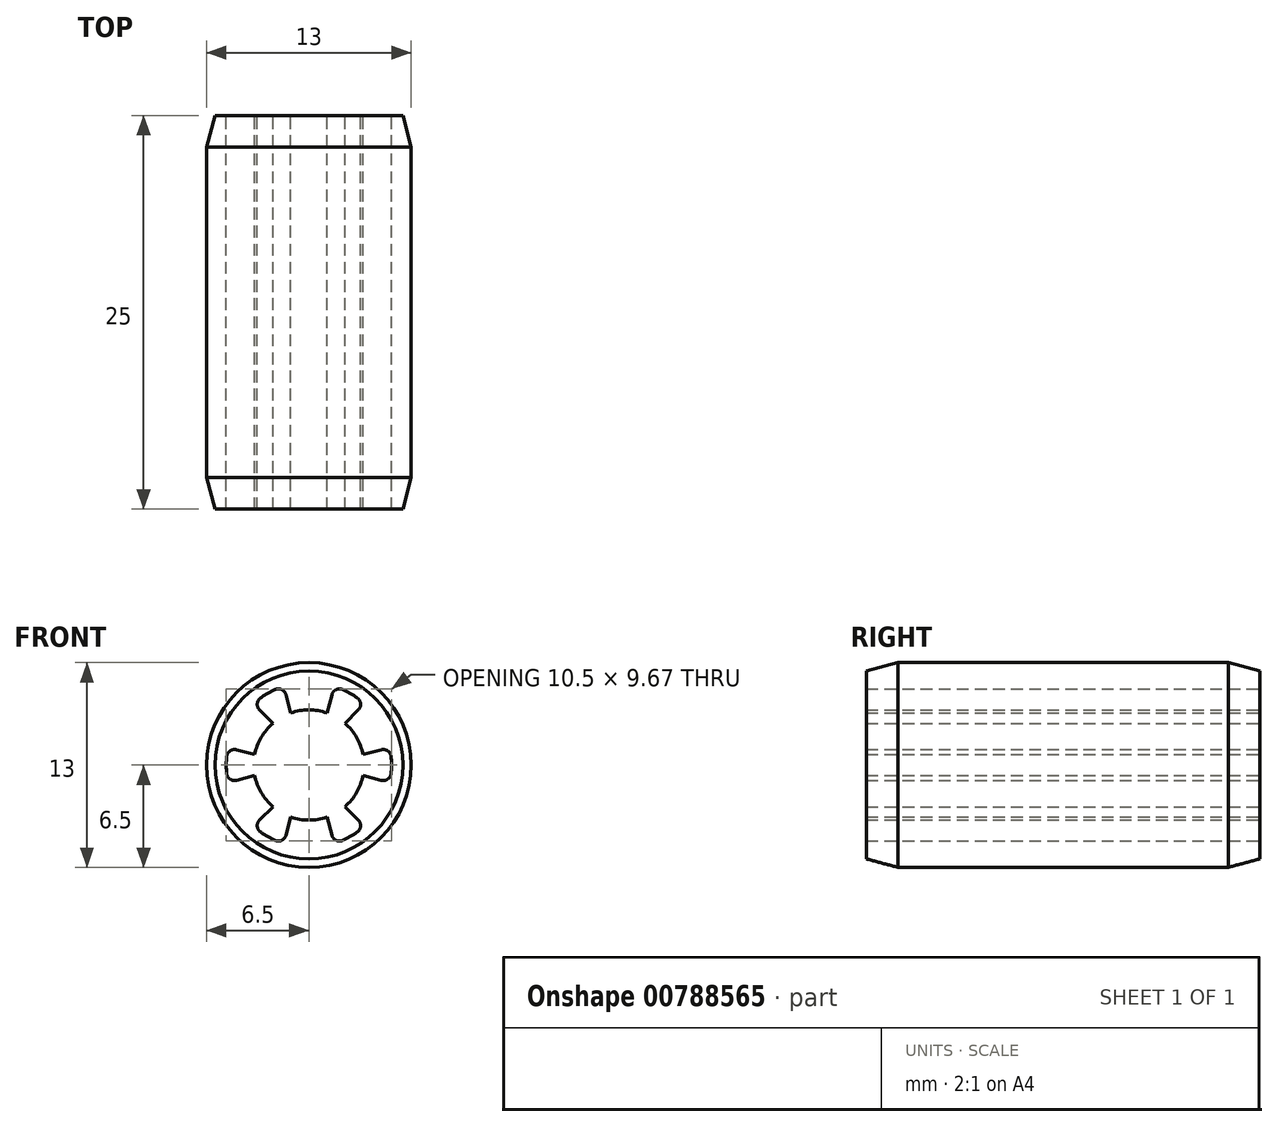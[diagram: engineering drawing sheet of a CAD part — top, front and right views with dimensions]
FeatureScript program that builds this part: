
annotation { "Feature Type Name" : "Feature", "Feature Type Description" : "" }
export const myFeature = defineFeature(function(context is Context, id is Id, definition is map)
    precondition{}
    {
        {
            var Q0;
            Q0=qCreatedBy(makeId("Front.planeOp"),FACE);
            var sketch = newSketch(context, id + "F0", { "sketchPlane" : qUnion([Q0])});
            skCircle(sketch, "E0", {"center": v(0, 0) * mm, "radius": 6.5 * mm});
            skCircle(sketch, "E1", {"center": v(0, 0) * mm, "radius": 5.25 * mm});
            skArc(sketch, "E2", {"start": v(-2.29, 2.65) * mm, "mid": v(-3.03, 1.75) * mm, "end": v(-3.44, 0.66) * mm});
            skLineSegment(sketch, "E3", {"start": v(1.6, 5) * mm, "end": v(1.15, 3.3) * mm});
            skLineSegment(sketch, "E4", {"start": v(-1.6, 5) * mm, "end": v(-1.15, 3.3) * mm});
            skLineSegment(sketch, "E5.1.0", {"start": v(-5.13, 1.11) * mm, "end": v(-3.44, 0.66) * mm});
            skLineSegment(sketch, "E5.1.1", {"start": v(-3.53, 3.89) * mm, "end": v(-2.29, 2.65) * mm});
            skLineSegment(sketch, "E5.2.0", {"start": v(-3.53, -3.89) * mm, "end": v(-2.29, -2.65) * mm});
            skLineSegment(sketch, "E5.2.1", {"start": v(-5.13, -1.11) * mm, "end": v(-3.44, -0.66) * mm});
            skLineSegment(sketch, "E5.3.0", {"start": v(1.6, -5) * mm, "end": v(1.15, -3.3) * mm});
            skLineSegment(sketch, "E5.3.1", {"start": v(-1.6, -5) * mm, "end": v(-1.15, -3.3) * mm});
            skLineSegment(sketch, "E5.4.0", {"start": v(5.13, -1.11) * mm, "end": v(3.44, -0.66) * mm});
            skLineSegment(sketch, "E5.4.1", {"start": v(3.53, -3.89) * mm, "end": v(2.29, -2.65) * mm});
            skLineSegment(sketch, "E5.5.0", {"start": v(3.53, 3.89) * mm, "end": v(2.29, 2.65) * mm});
            skLineSegment(sketch, "E5.5.1", {"start": v(5.13, 1.11) * mm, "end": v(3.44, 0.66) * mm});
            skArc(sketch, "E6.trimOffspring", {"start": v(1.15, 3.3) * mm, "mid": v(0, 3.5) * mm, "end": v(-1.15, 3.3) * mm});
            skArc(sketch, "E7.trimOffspring", {"start": v(3.44, 0.66) * mm, "mid": v(3.03, 1.75) * mm, "end": v(2.29, 2.65) * mm});
            skArc(sketch, "E8.trimOffspring", {"start": v(2.29, -2.65) * mm, "mid": v(3.03, -1.75) * mm, "end": v(3.44, -0.66) * mm});
            skArc(sketch, "E9.trimOffspring", {"start": v(-1.15, -3.3) * mm, "mid": v(0, -3.5) * mm, "end": v(1.15, -3.3) * mm});
            skArc(sketch, "E10.trimOffspring", {"start": v(-3.44, -0.66) * mm, "mid": v(-3.03, -1.75) * mm, "end": v(-2.29, -2.65) * mm});
            skSolve(sketch);
        }
        {
            var Q0;
            Q0=makeQuery(id+"F0.imprint","IMPRINT",FACE,{"disambiguationData":[TD([[makeQuery(id+"F0.imprint","IMPRINT",EDGE,{"derivedFrom":sQuery(id+"F0.wireOp",EDGE,"E0")}),1.0]])]});
            var Q1;
            {var subQ0=sQuery(id+"F0.wireOp",EDGE,"E3");Q1=makeQuery(id+"F0.imprint","IMPRINT",FACE,{"disambiguationData":[TD([[makeQuery(id+"F0.imprint","IMPRINT",EDGE,{"derivedFrom":subQ0}),-1.0]])]});}
            var Q2;
            {var subQ0=sQuery(id+"F0.wireOp",EDGE,"E5.5.0");Q2=makeQuery(id+"F0.imprint","IMPRINT",FACE,{"disambiguationData":[TD([[makeQuery(id+"F0.imprint","IMPRINT",EDGE,{"derivedFrom":subQ0}),1.0]])]});}
            var Q3;
            {var subQ0=sQuery(id+"F0.wireOp",EDGE,"E5.4.0");Q3=makeQuery(id+"F0.imprint","IMPRINT",FACE,{"disambiguationData":[TD([[makeQuery(id+"F0.imprint","IMPRINT",EDGE,{"derivedFrom":subQ0}),1.0]])]});}
            var Q4;
            {var subQ0=sQuery(id+"F0.wireOp",EDGE,"E5.3.0");Q4=makeQuery(id+"F0.imprint","IMPRINT",FACE,{"disambiguationData":[TD([[makeQuery(id+"F0.imprint","IMPRINT",EDGE,{"derivedFrom":subQ0}),1.0]])]});}
            var Q5;
            {var subQ0=sQuery(id+"F0.wireOp",EDGE,"E5.2.0");Q5=makeQuery(id+"F0.imprint","IMPRINT",FACE,{"disambiguationData":[TD([[makeQuery(id+"F0.imprint","IMPRINT",EDGE,{"derivedFrom":subQ0}),1.0]])]});}
            var Q6;
            Q6=makeQuery(id+"F0.imprint","IMPRINT",FACE,{"disambiguationData":[TD([[makeQuery(id+"F0.imprint","IMPRINT",EDGE,{"derivedFrom":sQuery(id+"F0.wireOp",EDGE,"E2")}),-1.0]])]});
            extrude(context, id + "F1", {"entities" : qUnion([Q0, Q1, Q2, Q3, Q4, Q5, Q6]), "depth" : 25 * mm, "offsetDistance" : 25 * mm});
        }
        {
            var Q0;
            Q0=makeQuery(id+"F1.opExtrude","SWEPT_EDGE",EDGE,{"disambiguationData":[OSD([sQuery(id+"F0.wireOp",EDGE,"E1"),sQuery(id+"F0.wireOp",EDGE,"E5.1.1")])]});
            var Q1;
            Q1=makeQuery(id+"F1.opExtrude","SWEPT_EDGE",EDGE,{"disambiguationData":[OSD([sQuery(id+"F0.wireOp",EDGE,"E1"),sQuery(id+"F0.wireOp",EDGE,"E4")])]});
            var Q2;
            Q2=makeQuery(id+"F1.opExtrude","SWEPT_EDGE",EDGE,{"disambiguationData":[OSD([sQuery(id+"F0.wireOp",EDGE,"E1"),sQuery(id+"F0.wireOp",EDGE,"E3")])]});
            var Q3;
            Q3=makeQuery(id+"F1.opExtrude","SWEPT_EDGE",EDGE,{"disambiguationData":[OSD([sQuery(id+"F0.wireOp",EDGE,"E1"),sQuery(id+"F0.wireOp",EDGE,"E5.5.0")])]});
            var Q4;
            Q4=makeQuery(id+"F1.opExtrude","SWEPT_EDGE",EDGE,{"disambiguationData":[OSD([sQuery(id+"F0.wireOp",EDGE,"E1"),sQuery(id+"F0.wireOp",EDGE,"E5.5.1")])]});
            var Q5;
            Q5=makeQuery(id+"F1.opExtrude","SWEPT_EDGE",EDGE,{"disambiguationData":[OSD([sQuery(id+"F0.wireOp",EDGE,"E1"),sQuery(id+"F0.wireOp",EDGE,"E5.4.0")])]});
            var Q6;
            Q6=makeQuery(id+"F1.opExtrude","SWEPT_EDGE",EDGE,{"disambiguationData":[OSD([sQuery(id+"F0.wireOp",EDGE,"E1"),sQuery(id+"F0.wireOp",EDGE,"E5.4.1")])]});
            var Q7;
            Q7=makeQuery(id+"F1.opExtrude","SWEPT_EDGE",EDGE,{"disambiguationData":[OSD([sQuery(id+"F0.wireOp",EDGE,"E1"),sQuery(id+"F0.wireOp",EDGE,"E5.3.0")])]});
            var Q8;
            Q8=makeQuery(id+"F1.opExtrude","SWEPT_EDGE",EDGE,{"disambiguationData":[OSD([sQuery(id+"F0.wireOp",EDGE,"E1"),sQuery(id+"F0.wireOp",EDGE,"E5.3.1")])]});
            var Q9;
            Q9=makeQuery(id+"F1.opExtrude","SWEPT_EDGE",EDGE,{"disambiguationData":[OSD([sQuery(id+"F0.wireOp",EDGE,"E1"),sQuery(id+"F0.wireOp",EDGE,"E5.2.0")])]});
            var Q10;
            Q10=makeQuery(id+"F1.opExtrude","SWEPT_EDGE",EDGE,{"disambiguationData":[OSD([sQuery(id+"F0.wireOp",EDGE,"E1"),sQuery(id+"F0.wireOp",EDGE,"E5.2.1")])]});
            var Q11;
            Q11=makeQuery(id+"F1.opExtrude","SWEPT_EDGE",EDGE,{"disambiguationData":[OSD([sQuery(id+"F0.wireOp",EDGE,"E1"),sQuery(id+"F0.wireOp",EDGE,"E5.1.0")])]});
            fillet(context, id + "F2", {"entities" : qUnion([Q0, Q1, Q2, Q3, Q4, Q5, Q6, Q7, Q8, Q9, Q10, Q11]), "radius" : 0.5 * mm, "tangentPropagation" : true, "allowEdgeOverflow" : false});
        }
        {
            var Q0;
            Q0=makeQuery(id+"F1.opExtrude","SWEPT_FACE",FACE,{"disambiguationData":[OSD([sQuery(id+"F0.wireOp",EDGE,"E0")])]});
            chamfer(context, id + "F3", {"entities" : qUnion([Q0]), "chamferType" : ChamferType.OFFSET_ANGLE, "width" : 2 * mm, "oppositeDirection" : false, "angle" : 15 * degree, "tangentPropagation" : true});
        }
    });
